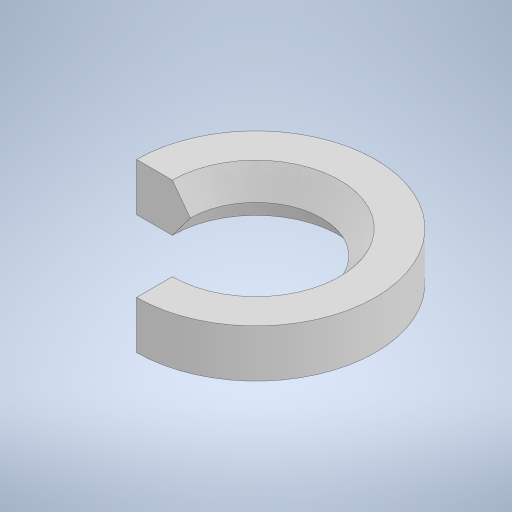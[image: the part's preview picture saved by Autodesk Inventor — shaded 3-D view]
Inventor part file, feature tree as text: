
AUTODESK INVENTOR PART (.ipt)
format: ipt  version: 2024 (Build 280153000, 153)  size: 248,320 bytes
history: native  units: mm
features: sketch x2, extrude x1, revolve x1
ambient origin geometry x8: Origin, YZ Plane, XZ Plane, XY Plane, X Axis, Y Axis, Z Axis, Center Point
bodies: Volumenkörper1 (feature_tree)
feature tree (4):
  extrude  "Extrusion1"  Depth=20.0mm
  revolve  "Umdrehung1"
  sketch  "Skizze1"  dims[d0=14.0mm d1=20.0mm]
  sketch  "Skizze2"  dims[d2=4.0mm d3=0.0mm d4=1.5mm d5=270.0deg]
